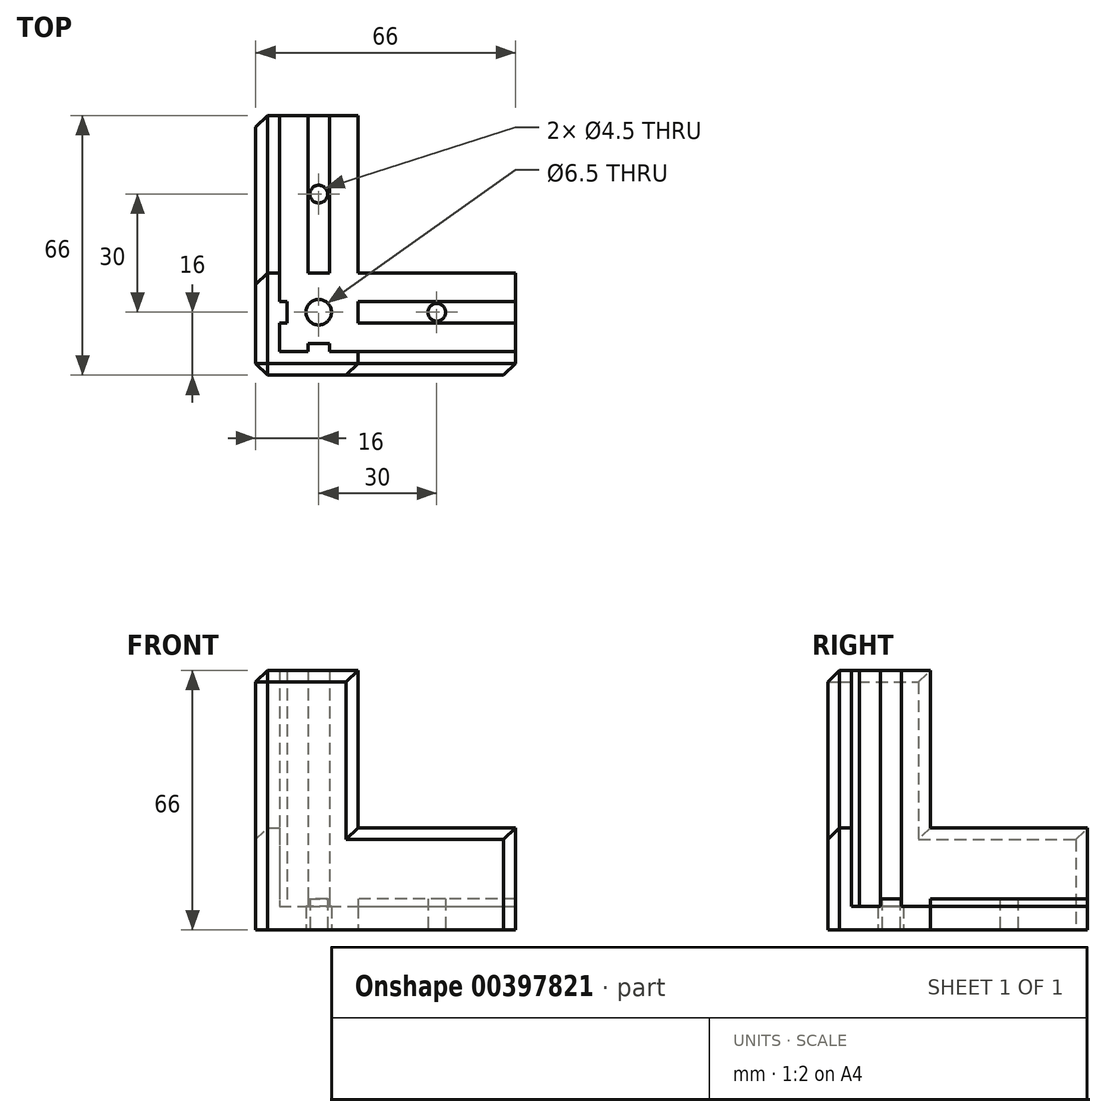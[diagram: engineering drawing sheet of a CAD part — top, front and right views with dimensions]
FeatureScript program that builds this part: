
annotation { "Feature Type Name" : "Feature", "Feature Type Description" : "" }
export const myFeature = defineFeature(function(context is Context, id is Id, definition is map)
    precondition{}
    {
        {
            var Q0;
            Q0=qCreatedBy(makeId("Top.planeOp"),FACE);
            var sketch = newSketch(context, id + "F0", { "sketchPlane" : qUnion([Q0])});
            skLineSegment(sketch, "E0", {"start": v(0, 0) * mm, "end": v(0, 66) * mm});
            skLineSegment(sketch, "E1", {"start": v(0, 66) * mm, "end": v(26, 66) * mm});
            skLineSegment(sketch, "E2", {"start": v(26, 66) * mm, "end": v(26, 26) * mm});
            skLineSegment(sketch, "E3", {"start": v(26, 26) * mm, "end": v(66, 26) * mm});
            skLineSegment(sketch, "E4", {"start": v(66, 26) * mm, "end": v(66, 0) * mm});
            skLineSegment(sketch, "E5", {"start": v(66, 0) * mm, "end": v(0, 0) * mm});
            skLineSegment(sketch, "E6", {"start": v(66, 6) * mm, "end": v(6, 6) * mm, "construction": true});
            skLineSegment(sketch, "E7", {"start": v(6, 6) * mm, "end": v(6, 66) * mm, "construction": true});
            skSolve(sketch);
        }
        {
            var Q0;
            Q0=qSketchRegion(id+"F0",true);
            extrude(context, id + "F1", {"entities" : qUnion([Q0]), "depth" : 6 * mm});
        }
        {
            var Q0;
            Q0=makeQuery(id+"F1.opExtrude","CAP_FACE",FACE,{"disambiguationData":[OSD([sQuery(id+"F0.wireOp",EDGE,"E0"),sQuery(id+"F0.wireOp",EDGE,"E1"),sQuery(id+"F0.wireOp",EDGE,"E2"),sQuery(id+"F0.wireOp",EDGE,"E3"),sQuery(id+"F0.wireOp",EDGE,"E4"),sQuery(id+"F0.wireOp",EDGE,"E5")])],"isStart":false});
            var sketch = newSketch(context, id + "F2", { "sketchPlane" : qUnion([Q0])});
            skLineSegment(sketch, "E8", {"start": v(0, 66) * mm, "end": v(6, 66) * mm});
            skLineSegment(sketch, "E9", {"start": v(6, 66) * mm, "end": v(6, 6) * mm});
            skLineSegment(sketch, "E10", {"start": v(6, 6) * mm, "end": v(66, 6) * mm});
            skLineSegment(sketch, "E11", {"start": v(66, 6) * mm, "end": v(66, 0) * mm});
            skLineSegment(sketch, "E12", {"start": v(66, 0) * mm, "end": v(0, 0) * mm});
            skLineSegment(sketch, "E13", {"start": v(0, 0) * mm, "end": v(0, 66) * mm});
            skSolve(sketch);
        }
        {
            var Q0;
            Q0=makeQuery(id+"F2.imprint","IMPRINT",FACE,{"disambiguationData":[TD([[makeQuery(id+"F2.imprint","IMPRINT",EDGE,{"derivedFrom":sQuery(id+"F2.wireOp",EDGE,"E8")}),-1.0]])]});
            extrude(context, id + "F3", {"entities" : qUnion([Q0]), "operationType" : NewBodyOperationType.ADD, "depth" : 20 * mm});
        }
        {
            var Q0;
            Q0=makeQuery(id+"F3.opExtrude","CAP_FACE",FACE,{"disambiguationData":[OSD([sQuery(id+"F2.wireOp",EDGE,"E8"),sQuery(id+"F2.wireOp",EDGE,"E9"),sQuery(id+"F2.wireOp",EDGE,"E10"),sQuery(id+"F2.wireOp",EDGE,"E11"),sQuery(id+"F2.wireOp",EDGE,"E12"),sQuery(id+"F2.wireOp",EDGE,"E13")])],"isStart":false});
            var sketch = newSketch(context, id + "F4", { "sketchPlane" : qUnion([Q0])});
            skLineSegment(sketch, "E14", {"start": v(6, 26) * mm, "end": v(0, 26) * mm});
            skLineSegment(sketch, "E15", {"start": v(0, 26) * mm, "end": v(0, 0) * mm});
            skLineSegment(sketch, "E16", {"start": v(0, 0) * mm, "end": v(26, 0) * mm});
            skLineSegment(sketch, "E17", {"start": v(26, 0) * mm, "end": v(26, 6) * mm});
            skLineSegment(sketch, "E18", {"start": v(26, 6) * mm, "end": v(6, 6) * mm});
            skLineSegment(sketch, "E19", {"start": v(6, 6) * mm, "end": v(6, 26) * mm});
            skSolve(sketch);
        }
        {
            var Q0;
            Q0=qSketchRegion(id+"F4",true);
            extrude(context, id + "F5", {"entities" : qUnion([Q0]), "operationType" : NewBodyOperationType.ADD, "depth" : 40 * mm});
        }
        {
            var Q0;
            Q0=makeQuery(id+"F1.opExtrude","CAP_FACE",FACE,{"disambiguationData":[OSD([sQuery(id+"F0.wireOp",EDGE,"E0"),sQuery(id+"F0.wireOp",EDGE,"E1"),sQuery(id+"F0.wireOp",EDGE,"E2"),sQuery(id+"F0.wireOp",EDGE,"E3"),sQuery(id+"F0.wireOp",EDGE,"E4"),sQuery(id+"F0.wireOp",EDGE,"E5")])],"isStart":false});
            var sketch = newSketch(context, id + "F6", { "sketchPlane" : qUnion([Q0])});
            skLineSegment(sketch, "E20", {"start": v(66, 16) * mm, "end": v(6, 16) * mm, "construction": true});
            skLineSegment(sketch, "E21", {"start": v(16, 66) * mm, "end": v(16, 6) * mm, "construction": true});
            skLineSegment(sketch, "E22", {"start": v(16, 6) * mm, "end": v(18.71, 6) * mm});
            skLineSegment(sketch, "E23", {"start": v(18.71, 6) * mm, "end": v(18.71, 8) * mm});
            skLineSegment(sketch, "E24", {"start": v(18.71, 8) * mm, "end": v(13.3, 8) * mm});
            skLineSegment(sketch, "E25", {"start": v(13.3, 8) * mm, "end": v(13.3, 6) * mm});
            skLineSegment(sketch, "E26", {"start": v(13.3, 6) * mm, "end": v(16, 6) * mm});
            skLineSegment(sketch, "E27", {"start": v(6, 16) * mm, "end": v(6, 18.7) * mm});
            skLineSegment(sketch, "E28", {"start": v(6, 18.7) * mm, "end": v(8, 18.7) * mm});
            skLineSegment(sketch, "E29", {"start": v(8, 18.7) * mm, "end": v(8, 13.29) * mm});
            skLineSegment(sketch, "E30", {"start": v(8, 13.29) * mm, "end": v(6, 13.29) * mm});
            skLineSegment(sketch, "E31", {"start": v(6, 13.29) * mm, "end": v(6, 16) * mm});
            skSolve(sketch);
        }
        {
            var Q0;
            Q0=qSketchRegion(id+"F6",true);
            extrude(context, id + "F7", {"entities" : qUnion([Q0]), "operationType" : NewBodyOperationType.ADD, "depth" : 60 * mm});
        }
        {
            var Q0;
            Q0=makeQuery(id+"F1.opExtrude","CAP_FACE",FACE,{"disambiguationData":[OSD([sQuery(id+"F0.wireOp",EDGE,"E0"),sQuery(id+"F0.wireOp",EDGE,"E1"),sQuery(id+"F0.wireOp",EDGE,"E2"),sQuery(id+"F0.wireOp",EDGE,"E3"),sQuery(id+"F0.wireOp",EDGE,"E4"),sQuery(id+"F0.wireOp",EDGE,"E5")])],"isStart":false});
            var sketch = newSketch(context, id + "F8", { "sketchPlane" : qUnion([Q0])});
            skLineSegment(sketch, "E32", {"start": v(66, 16) * mm, "end": v(8, 16) * mm, "construction": true});
            skLineSegment(sketch, "E33", {"start": v(66, 16) * mm, "end": v(66, 18.7) * mm});
            skLineSegment(sketch, "E34", {"start": v(66, 18.7) * mm, "end": v(26, 18.7) * mm});
            skLineSegment(sketch, "E35", {"start": v(26, 18.7) * mm, "end": v(26, 13.29) * mm});
            skLineSegment(sketch, "E36", {"start": v(26, 13.29) * mm, "end": v(66, 13.29) * mm});
            skLineSegment(sketch, "E37", {"start": v(66, 13.29) * mm, "end": v(66, 16) * mm});
            skLineSegment(sketch, "E38", {"start": v(16, 66) * mm, "end": v(16, 8) * mm, "construction": true});
            skLineSegment(sketch, "E39", {"start": v(16, 66) * mm, "end": v(13.3, 66) * mm});
            skLineSegment(sketch, "E40", {"start": v(13.3, 66) * mm, "end": v(13.3, 26) * mm});
            skLineSegment(sketch, "E41", {"start": v(13.3, 26) * mm, "end": v(18.7, 26) * mm});
            skLineSegment(sketch, "E42", {"start": v(18.7, 26) * mm, "end": v(18.7, 66) * mm});
            skLineSegment(sketch, "E43", {"start": v(18.7, 66) * mm, "end": v(16, 66) * mm});
            skSolve(sketch);
        }
        {
            var Q0;
            Q0=qSketchRegion(id+"F8",true);
            extrude(context, id + "F9", {"entities" : qUnion([Q0]), "operationType" : NewBodyOperationType.ADD, "depth" : 2 * mm});
        }
        {
            var Q0;
            Q0=makeQuery(id+"F5.boolean.opBoolean","MERGE",FACE,{"derivedFrom":[makeQuery(id+"F3.boolean.opBoolean","MERGE",FACE,{"derivedFrom":[makeQuery(id+"F1.opExtrude","SWEPT_FACE",FACE,{"disambiguationData":[OSD([sQuery(id+"F0.wireOp",EDGE,"E5")])]}),makeQuery(id+"F3.opExtrude","SWEPT_FACE",FACE,{"disambiguationData":[OSD([sQuery(id+"F2.wireOp",EDGE,"E12")])]})]}),makeQuery(id+"F5.opExtrude","SWEPT_FACE",FACE,{"disambiguationData":[OSD([sQuery(id+"F4.wireOp",EDGE,"E16")])]})]});
            var sketch = newSketch(context, id + "F10", { "sketchPlane" : qUnion([Q0])});
            skLineSegment(sketch, "E44", {"start": v(6, 66) * mm, "end": v(6, 6) * mm, "construction": true});
            skLineSegment(sketch, "E45", {"start": v(6, 6) * mm, "end": v(66, 6) * mm, "construction": true});
            skCircle(sketch, "E46", {"center": v(56, 16) * mm, "radius": 2.25 * mm});
            skCircle(sketch, "E47", {"center": v(36, 16) * mm, "radius": 2.25 * mm});
            skCircle(sketch, "E48", {"center": v(16, 56) * mm, "radius": 2.25 * mm});
            skLineSegment(sketch, "E49", {"start": v(26, 26) * mm, "end": v(6, 26) * mm, "construction": true});
            skLineSegment(sketch, "E50", {"start": v(26, 26) * mm, "end": v(26, 6) * mm, "construction": true});
            skSolve(sketch);
        }
        {
            var Q0;
            Q0=makeQuery(id+"F5.boolean.opBoolean","MERGE",FACE,{"derivedFrom":[makeQuery(id+"F3.boolean.opBoolean","MERGE",FACE,{"derivedFrom":[makeQuery(id+"F1.opExtrude","SWEPT_FACE",FACE,{"disambiguationData":[OSD([sQuery(id+"F0.wireOp",EDGE,"E0")])]}),makeQuery(id+"F3.opExtrude","SWEPT_FACE",FACE,{"disambiguationData":[OSD([sQuery(id+"F2.wireOp",EDGE,"E13")])]})]}),makeQuery(id+"F5.opExtrude","SWEPT_FACE",FACE,{"disambiguationData":[OSD([sQuery(id+"F4.wireOp",EDGE,"E15")])]})]});
            var sketch = newSketch(context, id + "F11", { "sketchPlane" : qUnion([Q0])});
            skLineSegment(sketch, "E51", {"start": v(-6, 66) * mm, "end": v(-6, 6) * mm, "construction": true});
            skLineSegment(sketch, "E52", {"start": v(-6, 6) * mm, "end": v(-66, 6) * mm, "construction": true});
            skCircle(sketch, "E53", {"center": v(-16, 56) * mm, "radius": 2.25 * mm});
            skCircle(sketch, "E54", {"center": v(-56, 16) * mm, "radius": 2.25 * mm});
            skCircle(sketch, "E55", {"center": v(-36, 16) * mm, "radius": 2.25 * mm});
            skSolve(sketch);
        }
        {
            var Q0;
            Q0=makeQuery(id+"F1.opExtrude","CAP_FACE",FACE,{"disambiguationData":[OSD([sQuery(id+"F0.wireOp",EDGE,"E0"),sQuery(id+"F0.wireOp",EDGE,"E1"),sQuery(id+"F0.wireOp",EDGE,"E2"),sQuery(id+"F0.wireOp",EDGE,"E3"),sQuery(id+"F0.wireOp",EDGE,"E4"),sQuery(id+"F0.wireOp",EDGE,"E5")])],"isStart":true});
            var sketch = newSketch(context, id + "F12", { "sketchPlane" : qUnion([Q0])});
            skLineSegment(sketch, "E56", {"start": v(66, -6) * mm, "end": v(6, -6) * mm, "construction": true});
            skLineSegment(sketch, "E57", {"start": v(6, -6) * mm, "end": v(6, -66) * mm, "construction": true});
            skCircle(sketch, "E58", {"center": v(16, -16) * mm, "radius": 3.25 * mm});
            skCircle(sketch, "E59", {"center": v(46, -16) * mm, "radius": 2.25 * mm});
            skCircle(sketch, "E60", {"center": v(16, -46) * mm, "radius": 2.25 * mm});
            skSolve(sketch);
        }
        {
            var Q0;
            Q0=qSketchRegion(id+"F12",true);
            extrude(context, id + "F13", {"entities" : qUnion([Q0]), "operationType" : NewBodyOperationType.REMOVE, "endBound" : BoundingType.UP_TO_NEXT, "oppositeDirection" : true, "depth" : 25 * mm});
        }
        {
            var Q0;
            Q0=makeQuery(id+"F5.boolean.opBoolean","MERGE",EDGE,{"derivedFrom":[makeQuery(id+"F3.boolean.opBoolean","MERGE",EDGE,{"derivedFrom":[makeQuery(id+"F1.opExtrude","SWEPT_EDGE",EDGE,{"disambiguationData":[OSD([sQuery(id+"F0.wireOp",EDGE,"E0"),sQuery(id+"F0.wireOp",EDGE,"E5")])]}),makeQuery(id+"F3.opExtrude","SWEPT_EDGE",EDGE,{"disambiguationData":[OSD([sQuery(id+"F2.wireOp",EDGE,"E12"),sQuery(id+"F2.wireOp",EDGE,"E13")])]})]}),makeQuery(id+"F5.opExtrude","SWEPT_EDGE",EDGE,{"disambiguationData":[OSD([sQuery(id+"F4.wireOp",EDGE,"E15"),sQuery(id+"F4.wireOp",EDGE,"E16")])]})]});
            var Q1;
            Q1=makeQuery(id+"F5.opExtrude","SWEPT_EDGE",EDGE,{"disambiguationData":[OSD([sQuery(id+"F2.wireOp",EDGE,"E13"),sQuery(id+"F4.wireOp",EDGE,"E14"),sQuery(id+"F4.wireOp",EDGE,"E15")])]});
            var Q2;
            Q2=makeQuery(id+"F3.opExtrude","CAP_EDGE",EDGE,{"disambiguationData":[OSD([sQuery(id+"F2.wireOp",EDGE,"E13")])],"isStart":false});
            var Q3;
            Q3=makeQuery(id+"F5.opExtrude","SWEPT_EDGE",EDGE,{"disambiguationData":[OSD([sQuery(id+"F2.wireOp",EDGE,"E12"),sQuery(id+"F4.wireOp",EDGE,"E16"),sQuery(id+"F4.wireOp",EDGE,"E17")])]});
            var Q4;
            Q4=makeQuery(id+"F3.opExtrude","CAP_EDGE",EDGE,{"disambiguationData":[OSD([sQuery(id+"F2.wireOp",EDGE,"E12")])],"isStart":false});
            var Q5;
            Q5=makeQuery(id+"F5.opExtrude","CAP_EDGE",EDGE,{"disambiguationData":[OSD([sQuery(id+"F4.wireOp",EDGE,"E15")])],"isStart":false});
            var Q6;
            Q6=makeQuery(id+"F5.opExtrude","CAP_EDGE",EDGE,{"disambiguationData":[OSD([sQuery(id+"F4.wireOp",EDGE,"E16")])],"isStart":false});
            var Q7;
            Q7=makeQuery(id+"F3.boolean.opBoolean","MERGE",EDGE,{"derivedFrom":[makeQuery(id+"F1.opExtrude","SWEPT_EDGE",EDGE,{"disambiguationData":[OSD([sQuery(id+"F0.wireOp",EDGE,"E0"),sQuery(id+"F0.wireOp",EDGE,"E1")])]}),makeQuery(id+"F3.opExtrude","SWEPT_EDGE",EDGE,{"disambiguationData":[OSD([sQuery(id+"F2.wireOp",EDGE,"E8"),sQuery(id+"F2.wireOp",EDGE,"E13")])]})]});
            var Q8;
            Q8=makeQuery(id+"F3.boolean.opBoolean","MERGE",EDGE,{"derivedFrom":[makeQuery(id+"F1.opExtrude","SWEPT_EDGE",EDGE,{"disambiguationData":[OSD([sQuery(id+"F0.wireOp",EDGE,"E4"),sQuery(id+"F0.wireOp",EDGE,"E5")])]}),makeQuery(id+"F3.opExtrude","SWEPT_EDGE",EDGE,{"disambiguationData":[OSD([sQuery(id+"F2.wireOp",EDGE,"E11"),sQuery(id+"F2.wireOp",EDGE,"E12")])]})]});
            chamfer(context, id + "F14", {"entities" : qUnion([Q0, Q1, Q2, Q3, Q4, Q5, Q6, Q7, Q8]), "width" : 3 * mm, "tangentPropagation" : true});
        }
    });
